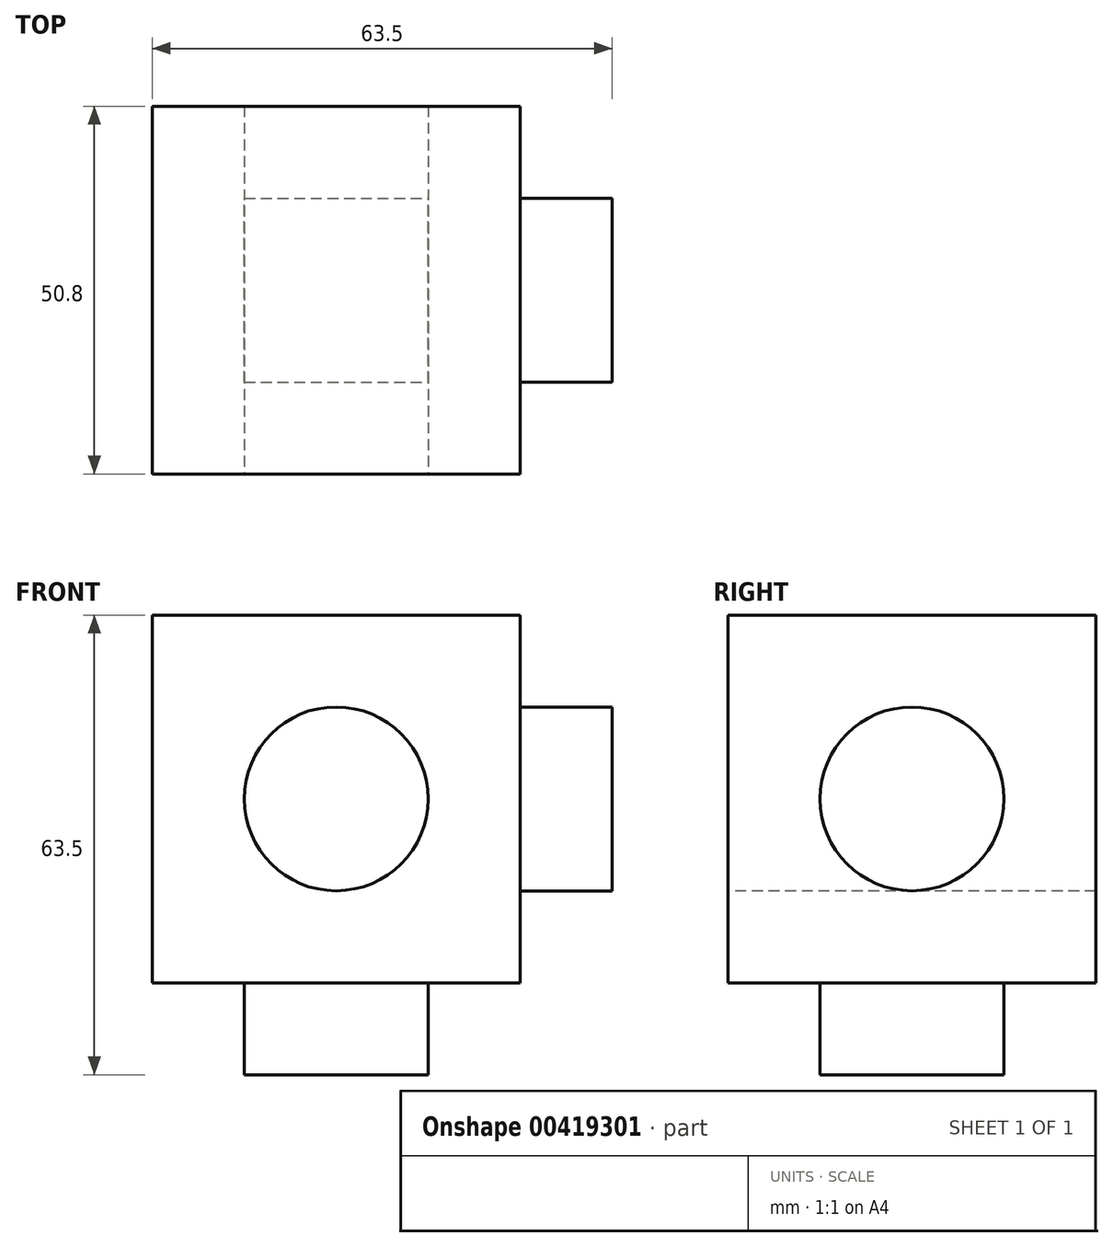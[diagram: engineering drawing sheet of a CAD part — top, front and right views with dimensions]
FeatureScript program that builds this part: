
annotation { "Feature Type Name" : "Feature", "Feature Type Description" : "" }
export const myFeature = defineFeature(function(context is Context, id is Id, definition is map)
    precondition{}
    {
        {
            var Q0;
            Q0=qCreatedBy(makeId("Front.planeOp"),FACE);
            var sketch = newSketch(context, id + "F0", { "sketchPlane" : qUnion([Q0])});
            skLineSegment(sketch, "E0.bottom", {"start": v(-29.15, 30.06) * mm, "end": v(21.65, 30.06) * mm});
            skLineSegment(sketch, "E0.top", {"start": v(-29.15, -20.74) * mm, "end": v(21.65, -20.74) * mm});
            skLineSegment(sketch, "E0.left", {"start": v(-29.15, 30.06) * mm, "end": v(-29.15, -20.74) * mm});
            skLineSegment(sketch, "E0.right", {"start": v(21.65, 30.06) * mm, "end": v(21.65, -20.74) * mm});
            skSolve(sketch);
        }
        {
            var Q0;
            Q0 = qSketchRegion(id + "F0", true);
            extrude(context, id + "F1", {"entities" : qUnion([Q0]), "depth" : 50.8 * mm});
        }
        {
            var Q0;
            Q0=makeQuery(id+"F1.opExtrude","CAP_FACE",FACE,{"disambiguationData":[OSD([sQuery(id+"F0.wireOp",EDGE,"E0.bottom"),sQuery(id+"F0.wireOp",EDGE,"E0.top"),sQuery(id+"F0.wireOp",EDGE,"E0.left"),sQuery(id+"F0.wireOp",EDGE,"E0.right")])],"isStart":false});
            var sketch = newSketch(context, id + "F2", { "sketchPlane" : qUnion([Q0])});
            skCircle(sketch, "E1", {"center": v(-3.75, 4.66) * mm, "radius": 12.7 * mm});
            skSolve(sketch);
        }
        {
            var Q0;
            Q0 = qSketchRegion(id + "F2", true);
            extrude(context, id + "F3", {"entities" : qUnion([Q0]), "operationType" : NewBodyOperationType.REMOVE, "oppositeDirection" : true, "depth" : 50.8 * mm});
        }
        {
            var Q0;
            Q0=makeQuery(id+"F1.opExtrude","SWEPT_FACE",FACE,{"disambiguationData":[OSD([sQuery(id+"F0.wireOp",EDGE,"E0.top")])]});
            var sketch = newSketch(context, id + "F4", { "sketchPlane" : qUnion([Q0])});
            skLineSegment(sketch, "E2.bottom", {"start": v(-16.45, 38.1) * mm, "end": v(8.95, 38.1) * mm});
            skLineSegment(sketch, "E2.top", {"start": v(-16.45, 12.7) * mm, "end": v(8.95, 12.7) * mm});
            skLineSegment(sketch, "E2.left", {"start": v(-16.45, 38.1) * mm, "end": v(-16.45, 12.7) * mm});
            skLineSegment(sketch, "E2.right", {"start": v(8.95, 38.1) * mm, "end": v(8.95, 12.7) * mm});
            skSolve(sketch);
        }
        {
            var Q0;
            Q0 = qSketchRegion(id + "F4", true);
            extrude(context, id + "F5", {"entities" : qUnion([Q0]), "operationType" : NewBodyOperationType.ADD, "depth" : 12.7 * mm});
        }
        {
            var Q0;
            Q0=makeQuery(id+"F1.opExtrude","SWEPT_FACE",FACE,{"disambiguationData":[OSD([sQuery(id+"F0.wireOp",EDGE,"E0.right")])]});
            var sketch = newSketch(context, id + "F6", { "sketchPlane" : qUnion([Q0])});
            skCircle(sketch, "E3", {"center": v(-25.4, 4.66) * mm, "radius": 12.7 * mm});
            skSolve(sketch);
        }
        {
            var Q0;
            Q0 = qSketchRegion(id + "F6", true);
            extrude(context, id + "F7", {"entities" : qUnion([Q0]), "operationType" : NewBodyOperationType.ADD, "depth" : 12.7 * mm});
        }
    });
